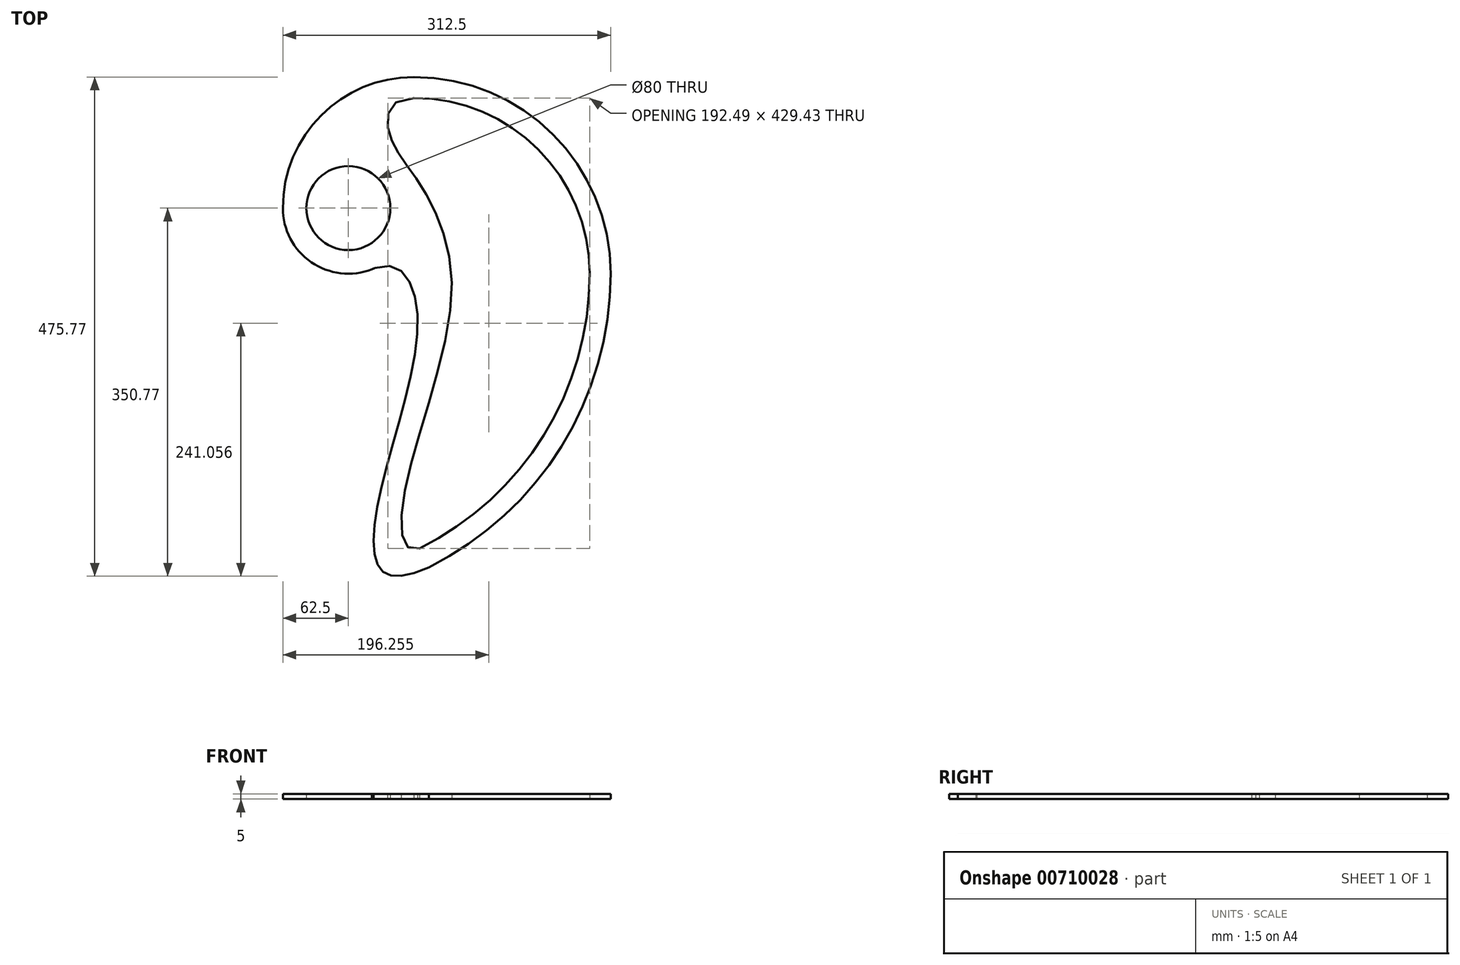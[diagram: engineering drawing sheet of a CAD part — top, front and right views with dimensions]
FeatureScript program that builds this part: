
annotation { "Feature Type Name" : "Feature", "Feature Type Description" : "" }
export const myFeature = defineFeature(function(context is Context, id is Id, definition is map)
    precondition{}
    {
        {
            var Q0;
            Q0=qCreatedBy(makeId("Top.planeOp"),FACE);
            var sketch = newSketch(context, id + "F0", { "sketchPlane" : qUnion([Q0])});
            skCircle(sketch, "E0", {"center": v(0, 0) * mm, "radius": 40 * mm});
            skArc(sketch, "E1", {"start": v(-62.5, 0) * mm, "mid": v(0, -62.5) * mm, "end": v(62.5, 0) * mm});
            skPoint(sketch, "E2", {"position": v(62.5, -62.5) * mm});
            skPoint(sketch, "E3", {"position": v(0, -62.5) * mm});
            skLineSegment(sketch, "E4.bottom", {"start": v(0, 0) * mm, "end": v(62.5, 0) * mm, "construction": true});
            skLineSegment(sketch, "E4.top", {"start": v(0, -62.5) * mm, "end": v(62.5, -62.5) * mm, "construction": true});
            skLineSegment(sketch, "E4.left", {"start": v(0, 0) * mm, "end": v(0, -62.5) * mm, "construction": true});
            skLineSegment(sketch, "E4.right", {"start": v(62.5, 0) * mm, "end": v(62.5, -62.5) * mm, "construction": true});
            skLineSegment(sketch, "E5.bottom", {"start": v(0, 0) * mm, "end": v(-62.5, 0) * mm, "construction": true});
            skLineSegment(sketch, "E5.top", {"start": v(0, -62.5) * mm, "end": v(-62.5, -62.5) * mm, "construction": true});
            skLineSegment(sketch, "E5.right", {"start": v(-62.5, 0) * mm, "end": v(-62.5, -62.5) * mm, "construction": true});
            skLineSegment(sketch, "E6.bottom", {"start": v(62.5, 0) * mm, "end": v(-62.5, 0) * mm, "construction": true});
            skLineSegment(sketch, "E6.top", {"start": v(62.5, 125) * mm, "end": v(-62.5, 125) * mm, "construction": true});
            skLineSegment(sketch, "E6.left", {"start": v(62.5, 0) * mm, "end": v(62.5, 125) * mm, "construction": true});
            skLineSegment(sketch, "E6.right", {"start": v(-62.5, 0) * mm, "end": v(-62.5, 125) * mm, "construction": true});
            skArc(sketch, "E7", {"start": v(-62.5, 0) * mm, "mid": v(-25.89, 88.39) * mm, "end": v(62.5, 125) * mm});
            skLineSegment(sketch, "E8.bottom", {"start": v(62.5, 125) * mm, "end": v(250, 125) * mm, "construction": true});
            skLineSegment(sketch, "E8.left", {"start": v(62.5, 125) * mm, "end": v(62.5, -62.5) * mm, "construction": true});
            skLineSegment(sketch, "E8.right", {"start": v(250, 125) * mm, "end": v(250, -62.5) * mm, "construction": true});
            skArc(sketch, "E9", {"start": v(62.5, 125) * mm, "mid": v(195.08, 70.08) * mm, "end": v(250, -62.5) * mm});
            skLineSegment(sketch, "E10.bottom", {"start": v(-62.5, -62.5) * mm, "end": v(62.5, -62.5) * mm, "construction": true});
            skLineSegment(sketch, "E10.top", {"start": v(-62.5, -375) * mm, "end": v(250, -375) * mm, "construction": true});
            skLineSegment(sketch, "E10.left", {"start": v(-62.5, -62.5) * mm, "end": v(-62.5, -375) * mm, "construction": true});
            skLineSegment(sketch, "E10.right", {"start": v(250, -62.5) * mm, "end": v(250, -375) * mm, "construction": true});
            skArc(sketch, "E11", {"start": v(250, -62.5) * mm, "mid": v(203.13, -227.1) * mm, "end": v(76.6, -342.34) * mm});
            skPoint(sketch, "E12.2.internal.snap0", {"position": v(31.25, -62.5) * mm});
            skPoint(sketch, "E12.3.internal.snap0", {"position": v(31.25, -62.5) * mm});
            skFitSpline(sketch, "E12", {"points": [v(22.46, -58.32) * mm, v(65.16, -94.03) * mm, v(31.25, -266.8) * mm, v(31.25, -344.93) * mm, v(76.6, -342.34) * mm], "startDerivative": vector(373.14, 169.22) * mm, "endDerivative": vector(354.13, 159.35) * mm});
            skArc(sketch, "E13.0", {"start": v(230, -62.5) * mm, "mid": v(186.13, -216.57) * mm, "end": v(67.7, -324.43) * mm});
            skArc(sketch, "E13.1", {"start": v(62.5, 105) * mm, "mid": v(180.94, 55.94) * mm, "end": v(230, -62.5) * mm});
            skFitSpline(sketch, "E14", {"points": [v(67.7, -324.43) * mm, v(51.34, -285.78) * mm, v(98.54, -76.64) * mm, v(62.5, 31.25) * mm, v(38.24, 74.03) * mm, v(62.5, 105) * mm], "startDerivative": vector(-324.23, -115.83) * mm, "endDerivative": vector(539.25, -8.96) * mm});
            skSolve(sketch);
        }
        {
            var Q0;
            Q0=makeQuery(id+"F0.imprint","IMPRINT",FACE,{"disambiguationData":[TD([[makeQuery(id+"F0.imprint","IMPRINT",EDGE,{"derivedFrom":sQuery(id+"F0.wireOp",EDGE,"E0")}),-1.0]])]});
            extrude(context, id + "F1", {"entities" : qUnion([Q0]), "depth" : 5 * mm, "offsetDistance" : 25 * mm});
        }
    });
